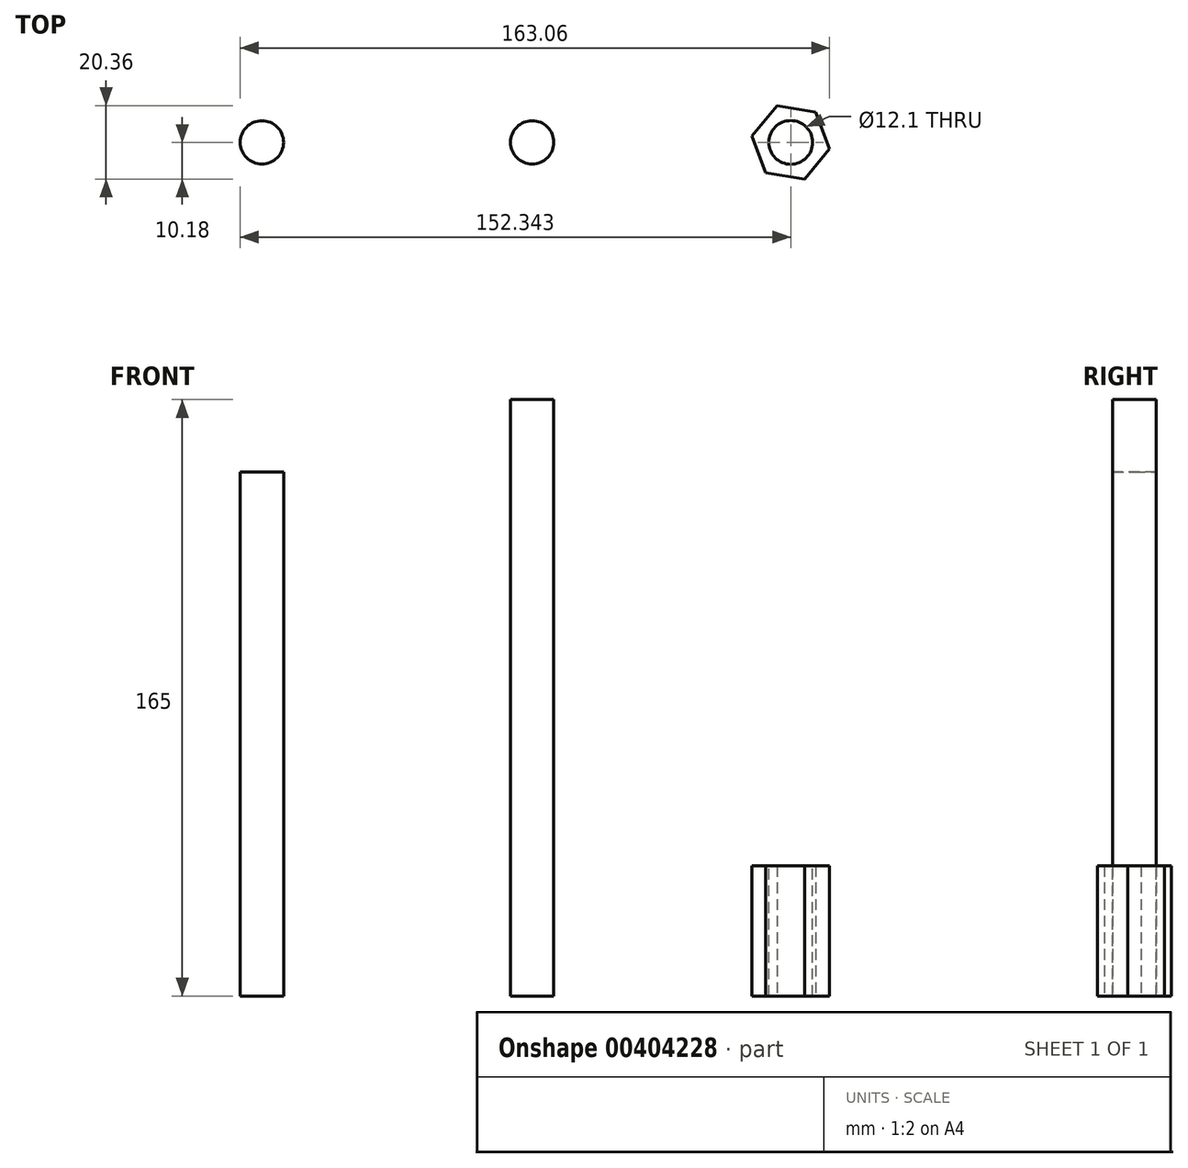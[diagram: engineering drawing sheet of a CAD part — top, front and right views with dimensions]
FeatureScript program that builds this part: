
annotation { "Feature Type Name" : "Feature", "Feature Type Description" : "" }
export const myFeature = defineFeature(function(context is Context, id is Id, definition is map)
    precondition{}
    {
        {
            var Q0;
            Q0=qCreatedBy(makeId("Top.planeOp"),FACE);
            var sketch = newSketch(context, id + "F0", { "sketchPlane" : qUnion([Q0])});
            skCircle(sketch, "E0", {"center": v(0, 0) * mm, "radius": 6 * mm});
            skCircle(sketch, "E1", {"center": v(74.78, 0) * mm, "radius": 6 * mm});
            skSolve(sketch);
        }
        {
            var Q0;
            Q0=makeQuery(id+"F0.imprint","IMPRINT",FACE,{"disambiguationData":[TD([[makeQuery(id+"F0.imprint","IMPRINT",EDGE,{"derivedFrom":sQuery(id+"F0.wireOp",EDGE,"E1")}),1.0]])]});
            extrude(context, id + "F1", {"entities" : qUnion([Q0]), "depth" : 165 * mm, "offsetDistance" : 25 * mm});
        }
        {
            var Q0;
            Q0 = qSketchRegion(id + "F0", true);
            extrude(context, id + "F2", {"entities" : qUnion([Q0]), "operationType" : NewBodyOperationType.ADD, "depth" : 145 * mm, "offsetDistance" : 25 * mm});
        }
        {
            var Q0;
            Q0=qCreatedBy(makeId("Top.planeOp"),FACE);
            var sketch = newSketch(context, id + "F3", { "sketchPlane" : qUnion([Q0])});
            skCircle(sketch, "E2.cCircle", {"center": v(146.34, 0) * mm, "radius": 10.87 * mm, "construction": true});
            skLineSegment(sketch, "E2.0", {"start": v(153.26, 8.38) * mm, "end": v(157.06, -1.8) * mm});
            skLineSegment(sketch, "E2.1", {"start": v(157.06, -1.8) * mm, "end": v(150.14, -10.18) * mm});
            skLineSegment(sketch, "E2.2", {"start": v(150.14, -10.18) * mm, "end": v(139.43, -8.38) * mm});
            skLineSegment(sketch, "E2.3", {"start": v(139.43, -8.38) * mm, "end": v(135.63, 1.8) * mm});
            skLineSegment(sketch, "E2.4", {"start": v(135.63, 1.8) * mm, "end": v(142.54, 10.18) * mm});
            skLineSegment(sketch, "E2.5", {"start": v(142.54, 10.18) * mm, "end": v(153.26, 8.38) * mm});
            skSolve(sketch);
        }
        {
            var Q0;
            Q0=makeQuery(id+"F3.imprint","IMPRINT",FACE,{"disambiguationData":[TD([[makeQuery(id+"F3.imprint","IMPRINT",EDGE,{"derivedFrom":sQuery(id+"F3.wireOp",EDGE,"E2.0")}),-1.0]])]});
            extrude(context, id + "F4", {"entities" : qUnion([Q0]), "depth" : 36 * mm, "offsetDistance" : 25 * mm});
        }
        {
            var Q0;
            Q0=sQuery(id+"F3.wireOp",VERTEX,"E2.cCircle.center");
            var Q1;
            Q1=makeQuery(id+"F4.opExtrude","SWEPT_BODY",BODY,{"disambiguationData":[OSD([sQuery(id+"F3.wireOp",EDGE,"E2.0"),sQuery(id+"F3.wireOp",EDGE,"E2.1"),sQuery(id+"F3.wireOp",EDGE,"E2.2"),sQuery(id+"F3.wireOp",EDGE,"E2.3"),sQuery(id+"F3.wireOp",EDGE,"E2.4"),sQuery(id+"F3.wireOp",EDGE,"E2.5")])]});
            hole(context, id + "F5", {"style" : HoleStyle.SIMPLE, "endStyle" : HoleEndStyle.THROUGH, "oppositeDirection" : true, "standardTappedOrClearance" : lookupTablePath({ "standard" : "ISO", "engagement" : "75%", "pitch" : "2 mm", "size" : "M14", "type" : "Tapped" }), "standardBlindInLast" : lookupTablePath({ "standard" : "ISO", "fit" : "Normal", "engagement" : "75%", "pitch" : "2 mm", "size" : "M14", "type" : "Clearance & tapped" }), "holeDiameter" : 12.1 * mm, "majorDiameter" : 14 * mm, "showTappedDepth" : true, "isTappedThrough" : true, "tappedDepth" : 11.2 * mm, "tapClearance" : 3, "startFromSketch" : true, "locations" : qUnion([Q0]), "scope" : qUnion([Q1])});
        }
    });
